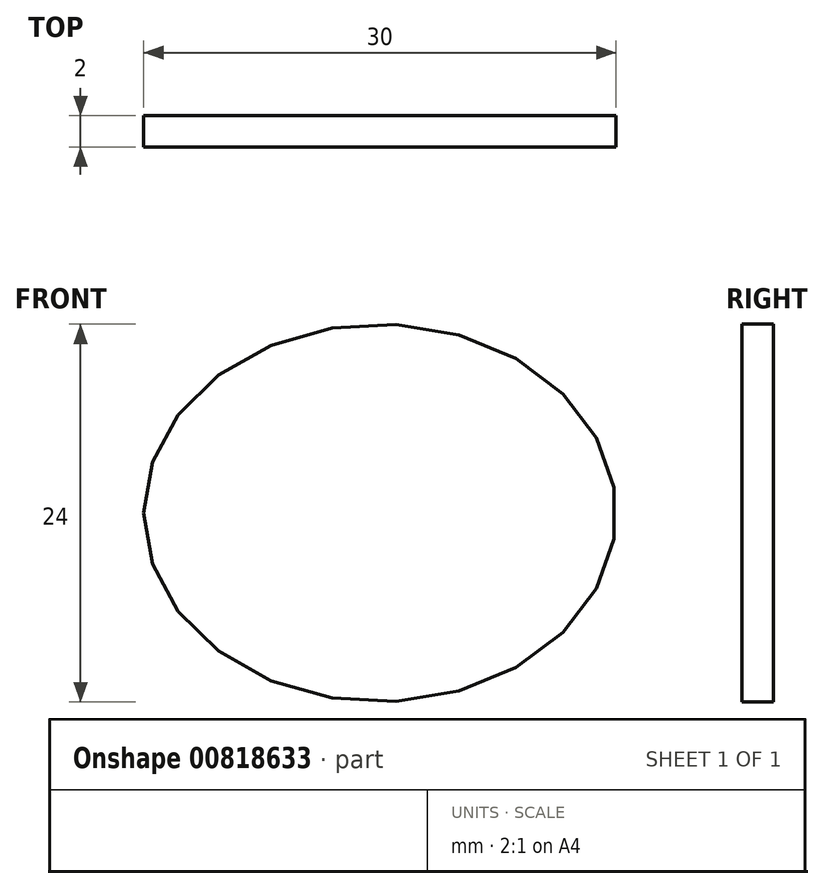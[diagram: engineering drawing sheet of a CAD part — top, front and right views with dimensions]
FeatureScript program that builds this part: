
annotation { "Feature Type Name" : "Feature", "Feature Type Description" : "" }
export const myFeature = defineFeature(function(context is Context, id is Id, definition is map)
    precondition{}
    {
        {
            var Q0;
            Q0=qCreatedBy(makeId("Front.planeOp"),FACE);
            var sketch = newSketch(context, id + "F0", { "sketchPlane" : qUnion([Q0])});
            skEllipse(sketch, "E0", {"center": v(0, 0) * mm, "majorRadius": 15 * mm, "minorRadius": 12 * mm, "majorAxis": v(-1, 0)});
            skFitSpline(sketch, "E1.0", {"points": [v(-24.9, 2.41) * mm, v(-25.05, 0) * mm, v(-24.9, -2.41) * mm, v(-24.31, -5.56) * mm, v(-23.18, -8.53) * mm, v(-21.58, -11.23) * mm, v(-19.7, -13.74) * mm, v(-16.94, -16.41) * mm, v(-13.76, -18.5) * mm, v(-11, -19.81) * mm, v(-8.18, -20.88) * mm, v(-5.25, -21.59) * mm, v(-2.27, -21.94) * mm, v(0, -22.03) * mm, v(2.27, -21.94) * mm, v(5.25, -21.59) * mm, v(8.18, -20.88) * mm, v(11, -19.81) * mm, v(13.76, -18.5) * mm, v(16.94, -16.41) * mm, v(19.7, -13.74) * mm, v(21.58, -11.23) * mm, v(23.18, -8.53) * mm, v(24.31, -5.56) * mm, v(24.9, -2.41) * mm, v(25.05, 0) * mm, v(24.9, 2.41) * mm, v(24.31, 5.56) * mm, v(23.18, 8.53) * mm, v(21.58, 11.23) * mm, v(19.7, 13.74) * mm, v(16.94, 16.41) * mm, v(13.76, 18.5) * mm, v(11, 19.81) * mm, v(8.18, 20.88) * mm, v(5.25, 21.59) * mm, v(2.27, 21.94) * mm, v(0, 22.03) * mm, v(-2.27, 21.94) * mm, v(-5.25, 21.59) * mm, v(-8.18, 20.88) * mm, v(-11, 19.81) * mm, v(-13.76, 18.5) * mm, v(-16.94, 16.41) * mm, v(-19.7, 13.74) * mm, v(-21.58, 11.23) * mm, v(-23.18, 8.53) * mm, v(-24.31, 5.56) * mm, v(-24.9, 2.41) * mm, v(-25.05, 0) * mm, v(-24.9, -2.41) * mm, v(-24.9, 2.41) * mm]});
            skSolve(sketch);
        }
        {
            var Q0;
            Q0 = qSketchRegion(id + "F0", true);
            extrude(context, id + "F1", {"entities" : qUnion([Q0]), "endBound" : BoundingType.SYMMETRIC, "depth" : 2 * mm, "offsetDistance" : 25 * mm});
        }
    });
